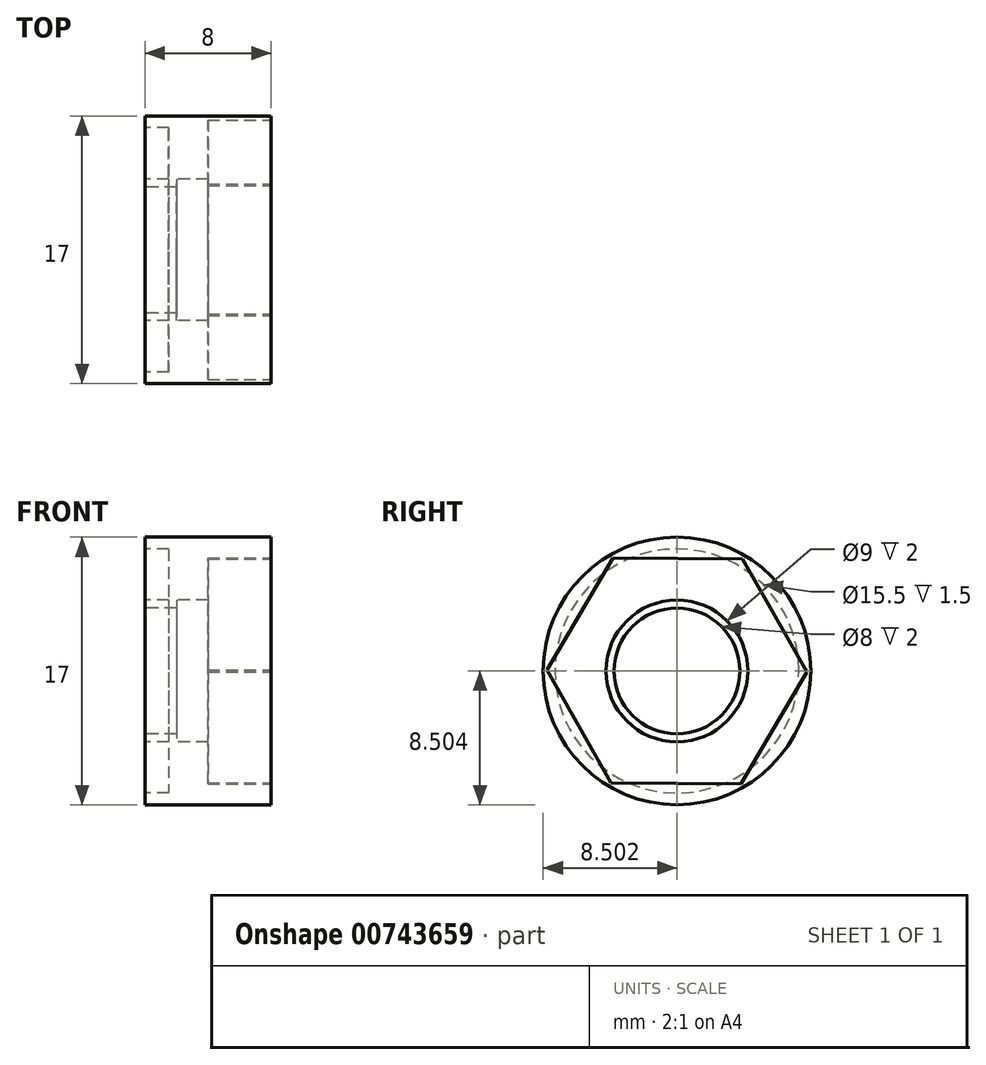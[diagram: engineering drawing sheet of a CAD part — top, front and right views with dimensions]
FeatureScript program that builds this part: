
annotation { "Feature Type Name" : "Feature", "Feature Type Description" : "" }
export const myFeature = defineFeature(function(context is Context, id is Id, definition is map)
    precondition{}
    {
        {
            var Q0;
            Q0=qCreatedBy(makeId("Right.planeOp"),FACE);
            var sketch = newSketch(context, id + "F0", { "sketchPlane" : qUnion([Q0])});
            skCircle(sketch, "E0", {"center": v(-39, 9.35) * mm, "radius": 8.5 * mm});
            skSolve(sketch);
        }
        {
            var Q0;
            Q0=makeQuery(id+"F0.imprint","IMPRINT",FACE,{"disambiguationData":[TD([[makeQuery(id+"F0.imprint","IMPRINT",EDGE,{"derivedFrom":sQuery(id+"F0.wireOp",EDGE,"E0")}),1.0]])]});
            extrude(context, id + "F1", {"entities" : qUnion([Q0]), "depth" : 8 * mm, "offsetDistance" : 25 * mm});
        }
        {
            var Q0;
            Q0=makeQuery(id+"F1.opExtrude","CAP_FACE",FACE,{"disambiguationData":[OSD([sQuery(id+"F0.wireOp",EDGE,"E0")])],"isStart":false});
            var sketch = newSketch(context, id + "F2", { "sketchPlane" : qUnion([Q0])});
            skLineSegment(sketch, "E1.0", {"start": v(-43.07, 16.53) * mm, "end": v(-34.82, 16.47) * mm});
            skLineSegment(sketch, "E1.1", {"start": v(-34.82, 16.47) * mm, "end": v(-30.75, 9.3) * mm});
            skLineSegment(sketch, "E1.2", {"start": v(-30.75, 9.3) * mm, "end": v(-34.92, 2.18) * mm});
            skLineSegment(sketch, "E1.3", {"start": v(-34.92, 2.18) * mm, "end": v(-43.17, 2.24) * mm});
            skLineSegment(sketch, "E1.4", {"start": v(-43.17, 2.24) * mm, "end": v(-47.25, 9.41) * mm});
            skLineSegment(sketch, "E1.5", {"start": v(-47.25, 9.41) * mm, "end": v(-43.07, 16.53) * mm});
            skSolve(sketch);
        }
        {
            var Q0;
            Q0=makeQuery(id+"F2.imprint","IMPRINT",FACE,{"disambiguationData":[TD([[makeQuery(id+"F2.imprint","IMPRINT",EDGE,{"derivedFrom":sQuery(id+"F2.wireOp",EDGE,"E1.0")}),-1.0]])]});
            extrude(context, id + "F3", {"entities" : qUnion([Q0]), "operationType" : NewBodyOperationType.REMOVE, "oppositeDirection" : true, "depth" : 4 * mm, "offsetDistance" : 25 * mm});
        }
        {
            var Q0;
            Q0=makeQuery(id+"F1.opExtrude","CAP_FACE",FACE,{"disambiguationData":[OSD([sQuery(id+"F0.wireOp",EDGE,"E0")])],"isStart":true});
            var sketch = newSketch(context, id + "F4", { "sketchPlane" : qUnion([Q0])});
            skCircle(sketch, "E2", {"center": v(39, 9.35) * mm, "radius": 7.75 * mm});
            skSolve(sketch);
        }
        {
            var Q0;
            Q0=makeQuery(id+"F4.imprint","IMPRINT",FACE,{"disambiguationData":[TD([[makeQuery(id+"F4.imprint","IMPRINT",EDGE,{"derivedFrom":sQuery(id+"F4.wireOp",EDGE,"E2")}),1.0]])]});
            extrude(context, id + "F5", {"entities" : qUnion([Q0]), "operationType" : NewBodyOperationType.REMOVE, "oppositeDirection" : true, "depth" : 1.5 * mm, "offsetDistance" : 25 * mm});
        }
        {
            var Q0;
            Q0=makeQuery(id+"F1.opExtrude","CAP_FACE",FACE,{"disambiguationData":[OSD([sQuery(id+"F0.wireOp",EDGE,"E0")])],"isStart":true});
            var sketch = newSketch(context, id + "F6", { "sketchPlane" : qUnion([Q0])});
            skCircle(sketch, "E3", {"center": v(39, 9.35) * mm, "radius": 4.5 * mm});
            skSolve(sketch);
        }
        {
            var Q0;
            Q0=makeQuery(id+"F6.imprint","IMPRINT",FACE,{"disambiguationData":[TD([[makeQuery(id+"F6.imprint","IMPRINT",EDGE,{"derivedFrom":sQuery(id+"F6.wireOp",EDGE,"E3")}),1.0]])]});
            var sketch = newSketch(context, id + "F7", { "sketchPlane" : qUnion([Q0])});
            skSolve(sketch);
        }
        {
            var Q0;
            Q0 = qSketchRegion(id + "F7", true);
            var Q1;
            Q1=makeQuery(id+"F7.imprint","IMPRINT",FACE,{"disambiguationData":[TD([[makeQuery(id+"F7.imprint","IMPRINT",EDGE,{"derivedFrom":makeQuery(id+"F6.imprint","IMPRINT",EDGE,{"derivedFrom":sQuery(id+"F6.wireOp",EDGE,"E3")})}),1.0]])]});
            extrude(context, id + "F8", {"entities" : qUnion([Q0, Q1]), "operationType" : NewBodyOperationType.REMOVE, "oppositeDirection" : true, "depth" : 25 * mm, "offsetDistance" : 25 * mm});
        }
        {
            var Q0;
            Q0=makeQuery(id+"F6.imprint","IMPRINT",FACE,{"disambiguationData":[TD([[makeQuery(id+"F6.imprint","IMPRINT",EDGE,{"derivedFrom":sQuery(id+"F6.wireOp",EDGE,"E3")}),1.0]])]});
            extrude(context, id + "F9", {"entities" : qUnion([Q0]), "operationType" : NewBodyOperationType.ADD, "oppositeDirection" : true, "depth" : 2 * mm, "offsetDistance" : 25 * mm});
        }
        {
            var Q0;
            Q0=makeQuery(id+"F9.opExtrude","CAP_FACE",FACE,{"disambiguationData":[OSD([sQuery(id+"F6.wireOp",EDGE,"E3")])],"isStart":true});
            var sketch = newSketch(context, id + "F10", { "sketchPlane" : qUnion([Q0])});
            skCircle(sketch, "E4", {"center": v(39, 9.35) * mm, "radius": 4 * mm});
            skSolve(sketch);
        }
        {
            var Q0;
            Q0=makeQuery(id+"F10.imprint","IMPRINT",FACE,{"disambiguationData":[TD([[makeQuery(id+"F10.imprint","IMPRINT",EDGE,{"derivedFrom":sQuery(id+"F10.wireOp",EDGE,"E4")}),1.0]])]});
            extrude(context, id + "F11", {"entities" : qUnion([Q0]), "operationType" : NewBodyOperationType.REMOVE, "oppositeDirection" : true, "depth" : 10 * mm, "offsetDistance" : 25 * mm});
        }
    });
